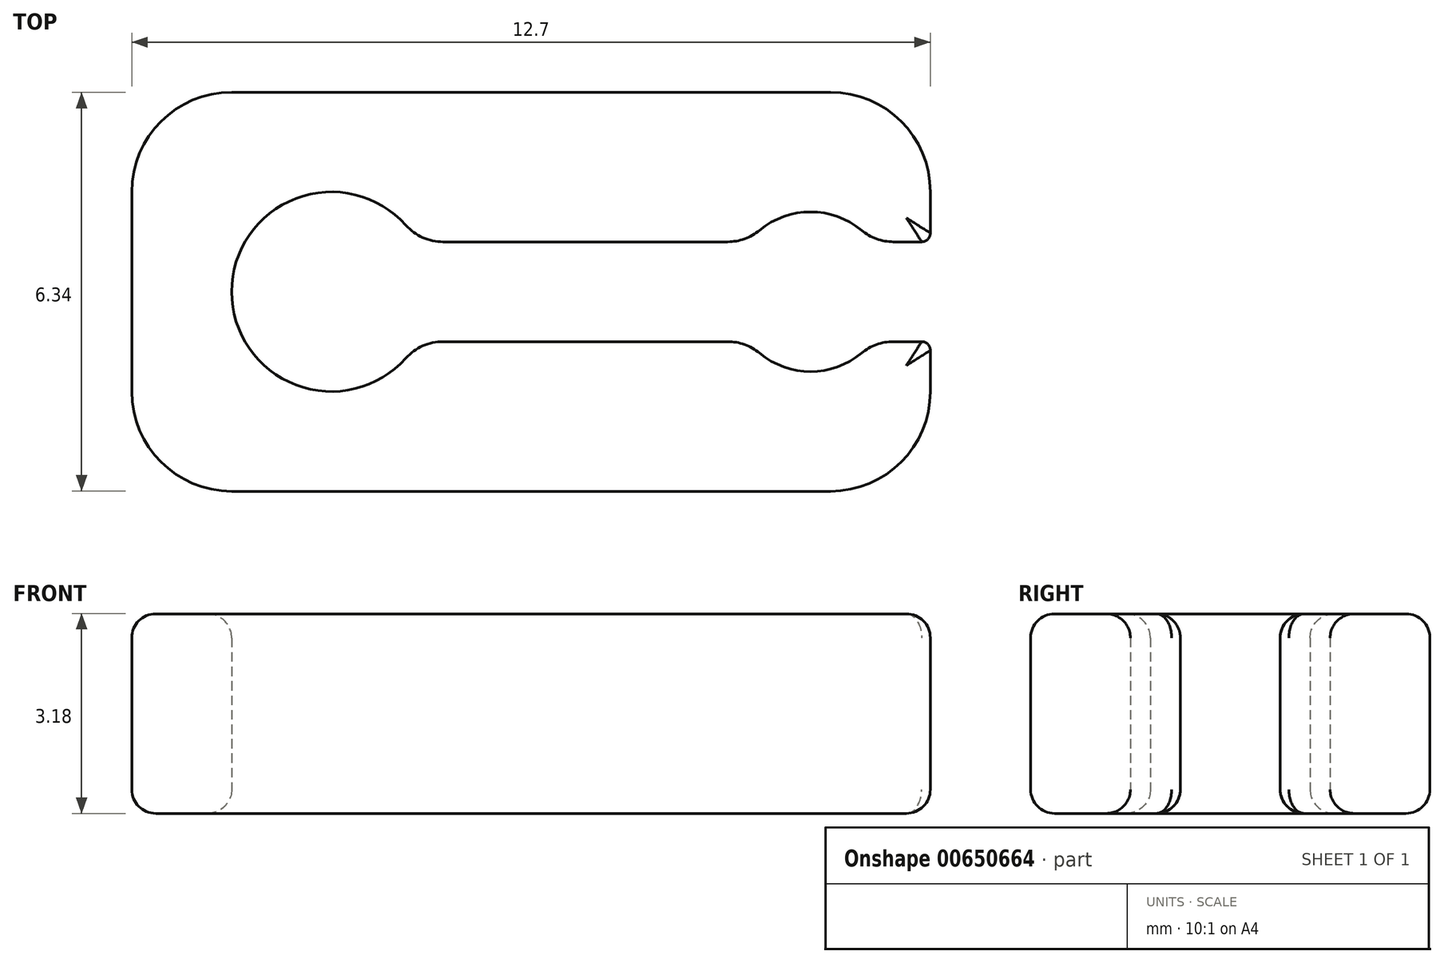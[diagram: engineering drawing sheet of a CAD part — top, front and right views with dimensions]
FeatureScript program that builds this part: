
annotation { "Feature Type Name" : "Feature", "Feature Type Description" : "" }
export const myFeature = defineFeature(function(context is Context, id is Id, definition is map)
    precondition{}
    {
        {
            var Q0;
            Q0=qCreatedBy(makeId("Top.planeOp"),FACE);
            var sketch = newSketch(context, id + "F0", { "sketchPlane" : qUnion([Q0])});
            skLineSegment(sketch, "E0.bottom", {"start": v(-4.76, 3.18) * mm, "end": v(4.76, 3.18) * mm});
            skLineSegment(sketch, "E0.top", {"start": v(-4.76, -3.18) * mm, "end": v(4.76, -3.18) * mm});
            skLineSegment(sketch, "E0.left", {"start": v(-6.35, 1.59) * mm, "end": v(-6.35, -1.59) * mm});
            skLineSegment(sketch, "E0.right", {"start": v(6.35, 1.59) * mm, "end": v(6.35, 0.93) * mm});
            skArc(sketch, "E1", {"start": v(-2, 1.06) * mm, "mid": v(-4.76, 0) * mm, "end": v(-2, -1.06) * mm});
            skLineSegment(sketch, "E2", {"start": v(-1.4, 0.8) * mm, "end": v(3.13, 0.8) * mm});
            skLineSegment(sketch, "E3", {"start": v(6.21, -0.8) * mm, "end": v(5.76, -0.8) * mm});
            skLineSegment(sketch, "E4.trimOffspring", {"start": v(6.35, -0.93) * mm, "end": v(6.35, -1.59) * mm});
            skArc(sketch, "E5", {"start": v(3.63, -0.98) * mm, "mid": v(4.45, -1.27) * mm, "end": v(5.26, -0.98) * mm});
            skLineSegment(sketch, "E6.trimOffspring", {"start": v(5.76, 0.8) * mm, "end": v(6.21, 0.8) * mm});
            skArc(sketch, "E7.trimOffspring", {"start": v(5.26, 0.98) * mm, "mid": v(4.45, 1.27) * mm, "end": v(3.63, 0.98) * mm});
            skLineSegment(sketch, "E8.trimOffspring", {"start": v(3.13, -0.8) * mm, "end": v(-1.4, -0.8) * mm});
            skPoint(sketch, "E9.visualSharp", {"position": v(-6.35, 3.18) * mm});
            skArc(sketch, "E9.filletArc", {"start": v(-4.76, 3.17) * mm, "mid": v(-5.89, 2.71) * mm, "end": v(-6.35, 1.59) * mm});
            skPoint(sketch, "E10.visualSharp", {"position": v(-6.35, -3.18) * mm});
            skArc(sketch, "E10.filletArc", {"start": v(-6.35, -1.59) * mm, "mid": v(-5.89, -2.71) * mm, "end": v(-4.76, -3.17) * mm});
            skPoint(sketch, "E11.visualSharp", {"position": v(6.35, -3.18) * mm});
            skArc(sketch, "E11.filletArc", {"start": v(4.76, -3.18) * mm, "mid": v(5.89, -2.71) * mm, "end": v(6.35, -1.59) * mm});
            skPoint(sketch, "E12.visualSharp", {"position": v(6.35, 3.18) * mm});
            skArc(sketch, "E12.filletArc", {"start": v(6.35, 1.59) * mm, "mid": v(5.89, 2.71) * mm, "end": v(4.76, 3.17) * mm});
            skPoint(sketch, "E13.visualSharp", {"position": v(-1.8, 0.8) * mm});
            skArc(sketch, "E13.filletArc", {"start": v(-2, 1.06) * mm, "mid": v(-1.72, 0.86) * mm, "end": v(-1.4, 0.8) * mm});
            skPoint(sketch, "E14.visualSharp", {"position": v(-1.8, -0.8) * mm});
            skArc(sketch, "E14.filletArc", {"start": v(-1.4, -0.8) * mm, "mid": v(-1.72, -0.86) * mm, "end": v(-2, -1.06) * mm});
            skPoint(sketch, "E15.visualSharp", {"position": v(3.45, -0.8) * mm});
            skArc(sketch, "E15.filletArc", {"start": v(3.63, -0.98) * mm, "mid": v(3.4, -0.84) * mm, "end": v(3.13, -0.8) * mm});
            skPoint(sketch, "E16.visualSharp", {"position": v(3.45, 0.8) * mm});
            skArc(sketch, "E16.filletArc", {"start": v(3.13, 0.8) * mm, "mid": v(3.4, 0.84) * mm, "end": v(3.63, 0.98) * mm});
            skPoint(sketch, "E17.visualSharp", {"position": v(5.44, 0.8) * mm});
            skArc(sketch, "E17.filletArc", {"start": v(5.26, 0.98) * mm, "mid": v(5.5, 0.84) * mm, "end": v(5.76, 0.8) * mm});
            skPoint(sketch, "E18.visualSharp", {"position": v(5.44, -0.8) * mm});
            skArc(sketch, "E18.filletArc", {"start": v(5.76, -0.8) * mm, "mid": v(5.5, -0.84) * mm, "end": v(5.26, -0.98) * mm});
            skPoint(sketch, "E19.visualSharp", {"position": v(6.35, 0.8) * mm});
            skArc(sketch, "E19.filletArc", {"start": v(6.21, 0.8) * mm, "mid": v(6.3, 0.83) * mm, "end": v(6.35, 0.93) * mm});
            skPoint(sketch, "E20.visualSharp", {"position": v(6.35, -0.8) * mm});
            skArc(sketch, "E20.filletArc", {"start": v(6.35, -0.93) * mm, "mid": v(6.3, -0.83) * mm, "end": v(6.21, -0.8) * mm});
            skSolve(sketch);
        }
        {
            var Q0;
            Q0 = qSketchRegion(id + "F0", true);
            extrude(context, id + "F1", {"entities" : qUnion([Q0]), "depth" : 3.17 * mm, "offsetDistance" : 25.4 * mm});
        }
        {
            var Q0;
            Q0=makeQuery(id+"F1.opExtrude","CAP_FACE",FACE,{"disambiguationData":[OSD([sQuery(id+"F0.wireOp",EDGE,"E0.bottom"),sQuery(id+"F0.wireOp",EDGE,"E0.top"),sQuery(id+"F0.wireOp",EDGE,"E0.left"),sQuery(id+"F0.wireOp",EDGE,"E0.right"),sQuery(id+"F0.wireOp",EDGE,"E1"),sQuery(id+"F0.wireOp",EDGE,"E2"),sQuery(id+"F0.wireOp",EDGE,"E3"),sQuery(id+"F0.wireOp",EDGE,"E4.trimOffspring"),sQuery(id+"F0.wireOp",EDGE,"E5"),sQuery(id+"F0.wireOp",EDGE,"E6.trimOffspring"),sQuery(id+"F0.wireOp",EDGE,"E7.trimOffspring"),sQuery(id+"F0.wireOp",EDGE,"E8.trimOffspring"),sQuery(id+"F0.wireOp",EDGE,"E9.filletArc"),sQuery(id+"F0.wireOp",EDGE,"E10.filletArc"),sQuery(id+"F0.wireOp",EDGE,"E11.filletArc"),sQuery(id+"F0.wireOp",EDGE,"E12.filletArc"),sQuery(id+"F0.wireOp",EDGE,"E13.filletArc"),sQuery(id+"F0.wireOp",EDGE,"E14.filletArc"),sQuery(id+"F0.wireOp",EDGE,"E15.filletArc"),sQuery(id+"F0.wireOp",EDGE,"E16.filletArc"),sQuery(id+"F0.wireOp",EDGE,"E17.filletArc"),sQuery(id+"F0.wireOp",EDGE,"E18.filletArc"),sQuery(id+"F0.wireOp",EDGE,"E19.filletArc"),sQuery(id+"F0.wireOp",EDGE,"E20.filletArc")])],"isStart":false});
            fillet(context, id + "F2", {"entities" : qUnion([Q0]), "radius" : 0.38 * mm, "tangentPropagation" : true, "allowEdgeOverflow" : false});
        }
        {
            var Q0;
            Q0=makeQuery(id+"F1.opExtrude","CAP_FACE",FACE,{"disambiguationData":[OSD([sQuery(id+"F0.wireOp",EDGE,"E0.bottom"),sQuery(id+"F0.wireOp",EDGE,"E0.top"),sQuery(id+"F0.wireOp",EDGE,"E0.left"),sQuery(id+"F0.wireOp",EDGE,"E0.right"),sQuery(id+"F0.wireOp",EDGE,"E1"),sQuery(id+"F0.wireOp",EDGE,"E2"),sQuery(id+"F0.wireOp",EDGE,"E3"),sQuery(id+"F0.wireOp",EDGE,"E4.trimOffspring"),sQuery(id+"F0.wireOp",EDGE,"E5"),sQuery(id+"F0.wireOp",EDGE,"E6.trimOffspring"),sQuery(id+"F0.wireOp",EDGE,"E7.trimOffspring"),sQuery(id+"F0.wireOp",EDGE,"E8.trimOffspring"),sQuery(id+"F0.wireOp",EDGE,"E9.filletArc"),sQuery(id+"F0.wireOp",EDGE,"E10.filletArc"),sQuery(id+"F0.wireOp",EDGE,"E11.filletArc"),sQuery(id+"F0.wireOp",EDGE,"E12.filletArc"),sQuery(id+"F0.wireOp",EDGE,"E13.filletArc"),sQuery(id+"F0.wireOp",EDGE,"E14.filletArc"),sQuery(id+"F0.wireOp",EDGE,"E15.filletArc"),sQuery(id+"F0.wireOp",EDGE,"E16.filletArc"),sQuery(id+"F0.wireOp",EDGE,"E17.filletArc"),sQuery(id+"F0.wireOp",EDGE,"E18.filletArc"),sQuery(id+"F0.wireOp",EDGE,"E19.filletArc"),sQuery(id+"F0.wireOp",EDGE,"E20.filletArc")])],"isStart":true});
            fillet(context, id + "F3", {"entities" : qUnion([Q0]), "radius" : 0.38 * mm, "tangentPropagation" : true, "allowEdgeOverflow" : false});
        }
    });
